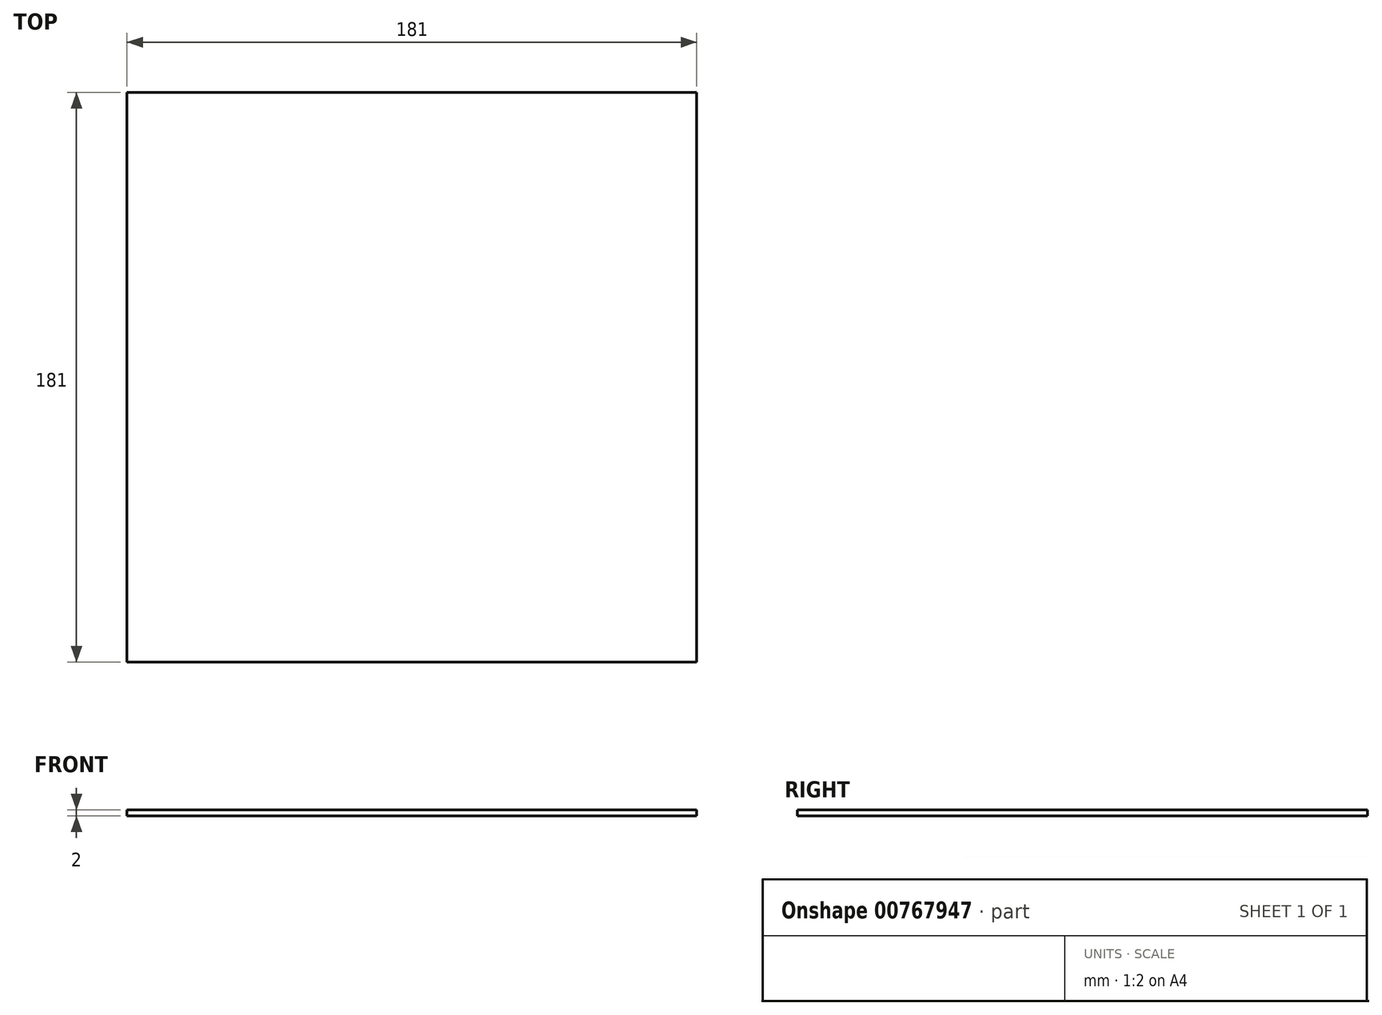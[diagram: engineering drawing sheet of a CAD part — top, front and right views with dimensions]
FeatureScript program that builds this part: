
annotation { "Feature Type Name" : "Feature", "Feature Type Description" : "" }
export const myFeature = defineFeature(function(context is Context, id is Id, definition is map)
    precondition{}
    {
        {
            var Q0;
            Q0=qCreatedBy(makeId("Top.planeOp"),FACE);
            var sketch = newSketch(context, id + "F0", { "sketchPlane" : qUnion([Q0])});
            skLineSegment(sketch, "E0.bottom", {"start": v(0, 0) * mm, "end": v(-181, 0) * mm});
            skLineSegment(sketch, "E0.top", {"start": v(0, -181) * mm, "end": v(-181, -181) * mm});
            skLineSegment(sketch, "E0.left", {"start": v(0, 0) * mm, "end": v(0, -181) * mm});
            skLineSegment(sketch, "E0.right", {"start": v(-181, 0) * mm, "end": v(-181, -181) * mm});
            skSolve(sketch);
        }
        {
            var Q0;
            Q0 = qSketchRegion(id + "F0", true);
            extrude(context, id + "F1", {"entities" : qUnion([Q0]), "depth" : 2 * mm, "offsetDistance" : 25 * mm});
        }
    });
